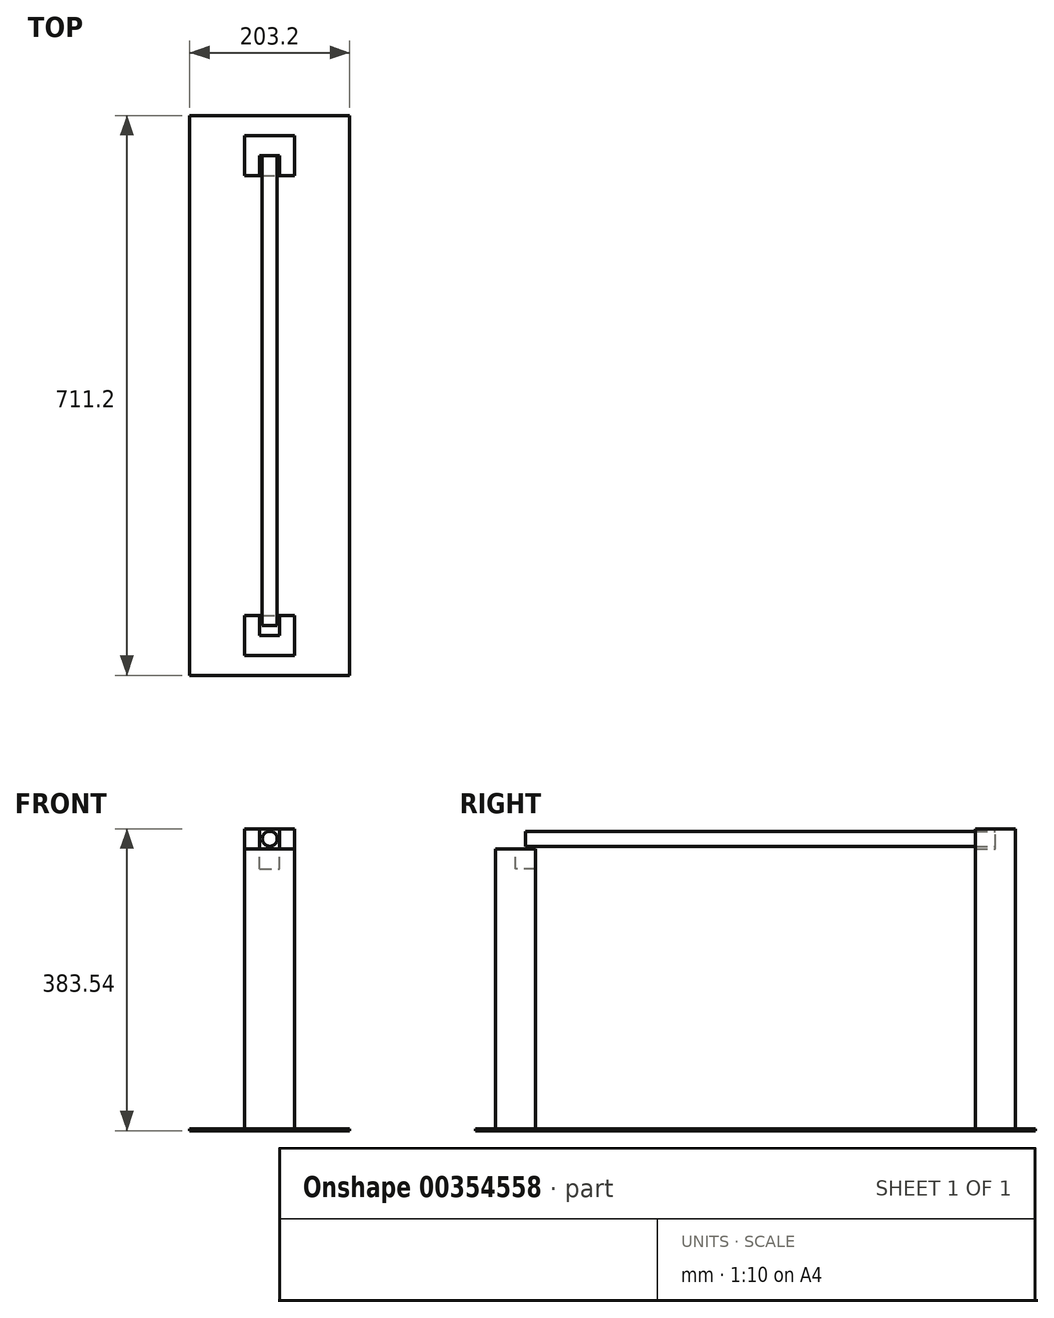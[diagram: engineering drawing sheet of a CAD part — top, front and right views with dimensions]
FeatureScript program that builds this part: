
annotation { "Feature Type Name" : "Feature", "Feature Type Description" : "" }
export const myFeature = defineFeature(function(context is Context, id is Id, definition is map)
    precondition{}
    {
        {
            var Q0;
            Q0=qCreatedBy(makeId("Top.planeOp"),FACE);
            var sketch = newSketch(context, id + "F0", { "sketchPlane" : qUnion([Q0])});
            skLineSegment(sketch, "E0.bottom", {"start": v(0, 0) * mm, "end": v(203.2, 0) * mm});
            skLineSegment(sketch, "E0.top", {"start": v(0, 711.2) * mm, "end": v(203.2, 711.2) * mm});
            skLineSegment(sketch, "E0.left", {"start": v(0, 0) * mm, "end": v(0, 711.2) * mm});
            skLineSegment(sketch, "E0.right", {"start": v(203.2, 0) * mm, "end": v(203.2, 711.2) * mm});
            skSolve(sketch);
        }
        {
            var Q0;
            Q0=makeQuery(id+"F0.imprint","IMPRINT",FACE,{"disambiguationData":[TD([[makeQuery(id+"F0.imprint","IMPRINT",EDGE,{"derivedFrom":sQuery(id+"F0.wireOp",EDGE,"E0.bottom")}),1.0]])]});
            extrude(context, id + "F1", {"entities" : qUnion([Q0]), "depth" : 2.54 * mm});
        }
        {
            var Q0;
            Q0=makeQuery(id+"F1.opExtrude","CAP_FACE",FACE,{"disambiguationData":[OSD([sQuery(id+"F0.wireOp",EDGE,"E0.bottom"),sQuery(id+"F0.wireOp",EDGE,"E0.top"),sQuery(id+"F0.wireOp",EDGE,"E0.left"),sQuery(id+"F0.wireOp",EDGE,"E0.right")])],"isStart":false});
            var sketch = newSketch(context, id + "F2", { "sketchPlane" : qUnion([Q0])});
            skLineSegment(sketch, "E1.bottom", {"start": v(69.85, 685.8) * mm, "end": v(133.35, 685.8) * mm});
            skLineSegment(sketch, "E1.top", {"start": v(69.85, 635) * mm, "end": v(133.35, 635) * mm});
            skLineSegment(sketch, "E1.left", {"start": v(69.85, 685.8) * mm, "end": v(69.85, 635) * mm});
            skLineSegment(sketch, "E1.right", {"start": v(133.35, 685.8) * mm, "end": v(133.35, 635) * mm});
            skLineSegment(sketch, "E2", {"start": v(101.6, 685.8) * mm, "end": v(101.6, 711.2) * mm, "construction": true});
            skLineSegment(sketch, "E3", {"start": v(0, 355.6) * mm, "end": v(203.2, 355.6) * mm, "construction": true});
            skLineSegment(sketch, "E4.MirrorCS", {"start": v(101.6, 25.4) * mm, "end": v(101.6, 0) * mm, "construction": true});
            skLineSegment(sketch, "E5.MirrorCS", {"start": v(133.35, 25.4) * mm, "end": v(133.35, 76.2) * mm});
            skLineSegment(sketch, "E6.MirrorCS", {"start": v(69.85, 25.4) * mm, "end": v(69.85, 76.2) * mm});
            skLineSegment(sketch, "E7.MirrorCS", {"start": v(69.85, 76.2) * mm, "end": v(133.35, 76.2) * mm});
            skLineSegment(sketch, "E8.MirrorCS", {"start": v(69.85, 25.4) * mm, "end": v(133.35, 25.4) * mm});
            skSolve(sketch);
        }
        {
            var Q0;
            Q0=makeQuery(id+"F2.imprint","IMPRINT",FACE,{"disambiguationData":[TD([[makeQuery(id+"F2.imprint","IMPRINT",EDGE,{"derivedFrom":sQuery(id+"F2.wireOp",EDGE,"E5.MirrorCS")}),1.0]])]});
            extrude(context, id + "F3", {"entities" : qUnion([Q0]), "operationType" : NewBodyOperationType.ADD, "depth" : 355.6 * mm});
        }
        {
            var Q0;
            Q0=makeQuery(id+"F2.imprint","IMPRINT",FACE,{"disambiguationData":[TD([[makeQuery(id+"F2.imprint","IMPRINT",EDGE,{"derivedFrom":sQuery(id+"F2.wireOp",EDGE,"E1.bottom")}),-1.0]])]});
            extrude(context, id + "F4", {"entities" : qUnion([Q0]), "operationType" : NewBodyOperationType.ADD, "depth" : 381 * mm});
        }
        {
            var Q0;
            Q0=makeQuery(id+"F3.opExtrude","CAP_FACE",FACE,{"disambiguationData":[OSD([sQuery(id+"F2.wireOp",EDGE,"E5.MirrorCS"),sQuery(id+"F2.wireOp",EDGE,"E6.MirrorCS"),sQuery(id+"F2.wireOp",EDGE,"E7.MirrorCS"),sQuery(id+"F2.wireOp",EDGE,"E8.MirrorCS")])],"isStart":false});
            var sketch = newSketch(context, id + "F5", { "sketchPlane" : qUnion([Q0])});
            skLineSegment(sketch, "E9.bottom", {"start": v(88.9, 76.2) * mm, "end": v(114.3, 76.2) * mm});
            skLineSegment(sketch, "E9.top", {"start": v(88.9, 50.8) * mm, "end": v(114.3, 50.8) * mm});
            skLineSegment(sketch, "E9.left", {"start": v(88.9, 76.2) * mm, "end": v(88.9, 50.8) * mm});
            skLineSegment(sketch, "E9.right", {"start": v(114.3, 76.2) * mm, "end": v(114.3, 50.8) * mm});
            skPoint(sketch, "E10", {"position": v(101.6, 76.2) * mm});
            skSolve(sketch);
        }
        {
            var Q0;
            Q0=makeQuery(id+"F5.imprint","IMPRINT",FACE,{"disambiguationData":[TD([[makeQuery(id+"F5.imprint","IMPRINT",EDGE,{"derivedFrom":sQuery(id+"F5.wireOp",EDGE,"E9.bottom")}),-1.0]])]});
            extrude(context, id + "F6", {"entities" : qUnion([Q0]), "operationType" : NewBodyOperationType.REMOVE, "oppositeDirection" : true, "depth" : 25.4 * mm});
        }
        {
            var Q0;
            Q0=makeQuery(id+"F4.opExtrude","CAP_FACE",FACE,{"disambiguationData":[OSD([sQuery(id+"F2.wireOp",EDGE,"E1.bottom"),sQuery(id+"F2.wireOp",EDGE,"E1.top"),sQuery(id+"F2.wireOp",EDGE,"E1.left"),sQuery(id+"F2.wireOp",EDGE,"E1.right")])],"isStart":false});
            var sketch = newSketch(context, id + "F7", { "sketchPlane" : qUnion([Q0])});
            skLineSegment(sketch, "E11.bottom", {"start": v(88.9, 635) * mm, "end": v(114.3, 635) * mm});
            skLineSegment(sketch, "E11.top", {"start": v(88.9, 660.4) * mm, "end": v(114.3, 660.4) * mm});
            skLineSegment(sketch, "E11.left", {"start": v(114.3, 635) * mm, "end": v(114.3, 660.4) * mm});
            skLineSegment(sketch, "E11.right", {"start": v(88.9, 635) * mm, "end": v(88.9, 660.4) * mm});
            skPoint(sketch, "E12", {"position": v(101.6, 635) * mm});
            skSolve(sketch);
        }
        {
            var Q0;
            Q0=makeQuery(id+"F7.imprint","IMPRINT",FACE,{"disambiguationData":[TD([[makeQuery(id+"F7.imprint","IMPRINT",EDGE,{"derivedFrom":sQuery(id+"F7.wireOp",EDGE,"E11.bottom")}),1.0]])]});
            extrude(context, id + "F8", {"entities" : qUnion([Q0]), "operationType" : NewBodyOperationType.REMOVE, "oppositeDirection" : true, "depth" : 25.4 * mm});
        }
        {
            var Q0;
            Q0=makeQuery(id+"F8.boolean.opBoolean","COPY",FACE,{"derivedFrom":makeQuery(id+"F8.opExtrude","SWEPT_FACE",FACE,{"disambiguationData":[OSD([sQuery(id+"F7.wireOp",EDGE,"E11.top")])]})});
            var sketch = newSketch(context, id + "F9", { "sketchPlane" : qUnion([Q0])});
            skCircle(sketch, "E13", {"center": v(101.6, 370.84) * mm, "radius": 9.53 * mm});
            skPoint(sketch, "E13.centerSnap0", {"position": v(114.3, 370.84) * mm});
            skPoint(sketch, "E13.centerSnap1", {"position": v(101.6, 383.54) * mm});
            skSolve(sketch);
        }
        {
            var Q0;
            Q0=makeQuery(id+"F9.imprint","IMPRINT",FACE,{"disambiguationData":[TD([[makeQuery(id+"F9.imprint","IMPRINT",EDGE,{"derivedFrom":sQuery(id+"F9.wireOp",EDGE,"E13")}),1.0]])]});
            extrude(context, id + "F10", {"entities" : qUnion([Q0]), "depth" : 596.9 * mm});
        }
    });
